# Revit family: 879-002X7X-001-DN450-600
name_source: partatom
category: Pipe Accessories
units: mm (PartAtom-declared; Revit-internal decimal feet)

## family parameters
Always vertical = Yes
Cut with Voids When Loaded = No
Part Type = Valve - Breaks Into
Round Connector Dimension = Use Diameter
Shared = No
Work Plane-Based = No

## types (48) — shared parameters
879-0450-00-04400207299 = DN450_PN10
879-0450-00-044002072A0 = DN450_PN10
879-0450-00-04400217299 = DN450_PN10
879-0450-00-044002172A0 = DN450_PN10
879-0450-00-04400227299 = DN450_PN10
879-0450-00-044002272A0 = DN450_PN10
879-0450-00-04400237299 = DN450_PN10
879-0450-00-044002372A0 = DN450_PN10
879-0450-00-14400207299 = DN450_PN16
879-0450-00-144002072A0 = DN450_PN16
879-0450-00-14400217299 = DN450_PN16
879-0450-00-144002172A0 = DN450_PN16
879-0450-00-14400227299 = DN450_PN16
879-0450-00-144002272A0 = DN450_PN16
879-0450-00-14400237299 = DN450_PN16
879-0450-00-144002372A0 = DN450_PN16
879-0500-00-04400207299 = DN500_PN10
879-0500-00-044002072A0 = DN500_PN10
879-0500-00-04400217299 = DN500_PN10
879-0500-00-044002172A0 = DN500_PN10
879-0500-00-04400227299 = DN500_PN10
879-0500-00-044002272A0 = DN500_PN10
879-0500-00-04400237299 = DN500_PN10
879-0500-00-044002372A0 = DN500_PN10
879-0500-00-14400207299 = DN500_PN16
879-0500-00-144002072A0 = DN500_PN16
879-0500-00-14400217299 = DN500_PN16
879-0500-00-144002172A0 = DN500_PN16
879-0500-00-14400227299 = DN500_PN16
879-0500-00-144002272A0 = DN500_PN16
879-0500-00-14400237299 = DN500_PN16
879-0500-00-144002372A0 = DN500_PN16
879-0600-00-04400207299 = DN600_PN10
879-0600-00-044002072A0 = DN600_PN10
879-0600-00-04400217299 = DN600_PN10
879-0600-00-044002172A0 = DN600_PN10
879-0600-00-04400227299 = DN600_PN10
879-0600-00-044002272A0 = DN600_PN10
879-0600-00-04400237299 = DN600_PN10
879-0600-00-044002372A0 = DN600_PN10
879-0600-00-14400207299 = DN600_PN16
879-0600-00-144002072A0 = DN600_PN16
879-0600-00-14400217299 = DN600_PN16
879-0600-00-144002172A0 = DN600_PN16
879-0600-00-14400227299 = DN600_PN16
879-0600-00-144002272A0 = DN600_PN16
879-0600-00-14400237299 = DN600_PN16
879-0600-00-144002372A0 = DN600_PN16
Body_wall_thickness = 10 mm  [stored 0.0328084 ft]
Bolt_support_Dia = 30 mm  [stored 0.0984252 ft]
Description_ = AVK CONST. FLOW/PRESS. RED. CONTROL VALVE
PG_depth = 21 mm  [stored 0.0688976 ft]
Profile_Dia = 15 mm  [stored 0.0492126 ft]
Profile_Dia_2 = 15 mm  [stored 0.0492126 ft]
Profile_Dia_3 = 30 mm  [stored 0.0984252 ft]
Search_Table = 879-002X7X-001-DN450-600
URL product pages = https://www.avkvalves.com

## per-type parameters (varying)
- 879-0450-00-04400207299_DN450_PN10: A=336.55 mm; Body_Collar_Dia=125 mm; Body_Collar_Dia_2=60 mm  [stored 0.19685 ft]; Body_Flange_Dia=315.79 mm; Body_Flange_Dia_2=324.32 mm; Body_Height_1=300 mm; Body_Height_2=150 mm; Body_Height_3=120 mm; Body_Height_4=165 mm; Body_Top_Dia=37.5 mm; Body_Top_Dia_2=31.25 mm  [stored 0.102526 ft]; Body_With_Dia=266.67 mm; Body_With_Dia_2=266.67 mm; Bolt_support=705.88 mm; Bolt_support_2=352.94 mm; Bolt_support_lenght=245 mm; Bolt_support_lenght_2=255 mm; Bottom_profile=112.5 mm; D1=265 mm; DN=450 mm; FOD=307.5 mm; Fillet_Length=20 mm  [stored 0.0656168 ft]; Flange_thickness=30 mm  [stored 0.0984252 ft]; H3=1060 mm; ID=225 mm; L=1200 mm; L1=1217 mm; L_Ref=1208.5 mm; L_ref_2=541.43 mm; PG_Dia=130 mm; PG_Ref=200 mm; PG_ref=235 mm; Pilot_Dia_1=75.5 mm; Pilot_Dia_1_Ref=90.6 mm; Pilot_Dia_1_Ref_2=181.2 mm; Pilot_Dia_2=143.45 mm; Pilot_Dia_3=50.33 mm; Pilot_Dia_4=25.17 mm; Pilot_Dia_5=16.78 mm; Pilot_top_1=678.75 mm; Pilot_top_ref=73.75 mm  [stored 0.241962 ft]; Profile1_Height=509 mm; Profile1_Length=96.09 mm; Profile1_Length_2=64.06 mm; Top_Profile=423.53 mm; Top_Profile_Ref=428.53 mm; Top_Ref=605 mm; Top_Ref_2=641.88 mm; W=780 mm; W_Ref=636.55 mm
- 879-0450-00-044002072A0_DN450_PN10: A=336.55 mm; Body_Collar_Dia=125 mm; Body_Collar_Dia_2=60 mm  [stored 0.19685 ft]; Body_Flange_Dia=315.79 mm; Body_Flange_Dia_2=324.32 mm; Body_Height_1=300 mm; Body_Height_2=150 mm; Body_Height_3=120 mm; Body_Height_4=165 mm; Body_Top_Dia=37.5 mm; Body_Top_Dia_2=31.25 mm  [stored 0.102526 ft]; Body_With_Dia=266.67 mm; Body_With_Dia_2=266.67 mm; Bolt_support=705.88 mm; Bolt_support_2=352.94 mm; Bolt_support_lenght=245.05 mm; Bolt_support_lenght_2=255.05 mm; Bottom_profile=112.53 mm; D1=265 mm; DN=450.1 mm; FOD=307.5 mm; Fillet_Length=20 mm  [stored 0.0656168 ft]; Flange_thickness=30 mm  [stored 0.0984252 ft]; H3=1220 mm; ID=225.05 mm; L=1200 mm; L1=1217 mm; L_Ref=1208.5 mm; L_ref_2=541.43 mm; PG_Dia=130 mm; PG_Ref=200 mm; PG_ref=235.05 mm; Pilot_Dia_1=75.5 mm; Pilot_Dia_1_Ref=90.6 mm; Pilot_Dia_1_Ref_2=181.2 mm; Pilot_Dia_2=143.45 mm; Pilot_Dia_3=50.33 mm; Pilot_Dia_4=25.17 mm; Pilot_Dia_5=16.78 mm; Pilot_top_1=758.75 mm; Pilot_top_ref=153.75 mm; Profile1_Height=530.5 mm; Profile1_Length=96.09 mm; Profile1_Length_2=64.06 mm; Top_Profile=423.53 mm; Top_Profile_Ref=428.53 mm; Top_Ref=605 mm; Top_Ref_2=681.88 mm; W=780 mm; W_Ref=636.55 mm
- 879-0450-00-04400217299_DN450_PN10: A=329.9 mm; Body_Collar_Dia=125 mm; Body_Collar_Dia_2=60 mm  [stored 0.19685 ft]; Body_Flange_Dia=315.79 mm; Body_Flange_Dia_2=324.32 mm; Body_Height_1=300 mm; Body_Height_2=150 mm; Body_Height_3=120 mm; Body_Height_4=165 mm; Body_Top_Dia=37.5 mm; Body_Top_Dia_2=31.25 mm  [stored 0.102526 ft]; Body_With_Dia=266.67 mm; Body_With_Dia_2=266.67 mm; Bolt_support=705.88 mm; Bolt_support_2=352.94 mm; Bolt_support_lenght=245.1 mm; Bolt_support_lenght_2=255.1 mm; Bottom_profile=112.55 mm; D1=265 mm; DN=450.2 mm; FOD=307.5 mm; Fillet_Length=20 mm  [stored 0.0656168 ft]; Flange_thickness=30 mm  [stored 0.0984252 ft]; H3=1060 mm; ID=225.1 mm; L=1200 mm; L1=1217 mm; L_Ref=1208.5 mm; L_ref_2=541.43 mm; PG_Dia=130 mm; PG_Ref=200 mm; PG_ref=235.1 mm; Pilot_Dia_1=79 mm; Pilot_Dia_1_Ref=94.8 mm; Pilot_Dia_1_Ref_2=189.6 mm; Pilot_Dia_2=150.1 mm; Pilot_Dia_3=52.67 mm; Pilot_Dia_4=26.33 mm; Pilot_Dia_5=17.56 mm; Pilot_top_1=678.75 mm; Pilot_top_ref=73.75 mm  [stored 0.241962 ft]; Profile1_Height=530 mm; Profile1_Length=96.09 mm; Profile1_Length_2=64.06 mm; Top_Profile=423.53 mm; Top_Profile_Ref=428.53 mm; Top_Ref=605 mm; Top_Ref_2=641.88 mm; W=780 mm; W_Ref=629.9 mm
- 879-0450-00-044002172A0_DN450_PN10: A=329.9 mm; Body_Collar_Dia=125 mm; Body_Collar_Dia_2=60 mm  [stored 0.19685 ft]; Body_Flange_Dia=315.79 mm; Body_Flange_Dia_2=324.32 mm; Body_Height_1=300 mm; Body_Height_2=150 mm; Body_Height_3=120 mm; Body_Height_4=165 mm; Body_Top_Dia=37.5 mm; Body_Top_Dia_2=31.25 mm  [stored 0.102526 ft]; Body_With_Dia=266.67 mm; Body_With_Dia_2=266.67 mm; Bolt_support=705.88 mm; Bolt_support_2=352.94 mm; Bolt_support_lenght=245.15 mm; Bolt_support_lenght_2=255.15 mm; Bottom_profile=112.58 mm; D1=265 mm; DN=450.3 mm; FOD=307.5 mm; Fillet_Length=20 mm  [stored 0.0656168 ft]; Flange_thickness=30 mm  [stored 0.0984252 ft]; H3=1220 mm; ID=225.15 mm; L=1200 mm; L1=1217 mm; L_Ref=1208.5 mm; L_ref_2=541.43 mm; PG_Dia=130 mm; PG_Ref=200 mm; PG_ref=235.15 mm; Pilot_Dia_1=79 mm; Pilot_Dia_1_Ref=94.8 mm; Pilot_Dia_1_Ref_2=189.6 mm; Pilot_Dia_2=150.1 mm; Pilot_Dia_3=52.67 mm; Pilot_Dia_4=26.33 mm; Pilot_Dia_5=17.56 mm; Pilot_top_1=758.75 mm; Pilot_top_ref=153.75 mm; Profile1_Height=530.5 mm; Profile1_Length=96.09 mm; Profile1_Length_2=64.06 mm; Top_Profile=423.53 mm; Top_Profile_Ref=428.53 mm; Top_Ref=605 mm; Top_Ref_2=681.88 mm; W=780 mm; W_Ref=629.9 mm
- 879-0450-00-04400227299_DN450_PN10: A=336.55 mm; Body_Collar_Dia=125 mm; Body_Collar_Dia_2=60 mm  [stored 0.19685 ft]; Body_Flange_Dia=315.79 mm; Body_Flange_Dia_2=324.32 mm; Body_Height_1=300 mm; Body_Height_2=150 mm; Body_Height_3=120 mm; Body_Height_4=165 mm; Body_Top_Dia=37.5 mm; Body_Top_Dia_2=31.25 mm  [stored 0.102526 ft]; Body_With_Dia=266.67 mm; Body_With_Dia_2=266.67 mm; Bolt_support=705.88 mm; Bolt_support_2=352.94 mm; Bolt_support_lenght=245.2 mm; Bolt_support_lenght_2=255.2 mm; Bottom_profile=112.6 mm; D1=265 mm; DN=450.4 mm; FOD=307.5 mm; Fillet_Length=20 mm  [stored 0.0656168 ft]; Flange_thickness=30 mm  [stored 0.0984252 ft]; H3=1060 mm; ID=225.2 mm; L=1200 mm; L1=1217 mm; L_Ref=1208.5 mm; L_ref_2=541.43 mm; PG_Dia=130 mm; PG_Ref=200 mm; PG_ref=235.2 mm; Pilot_Dia_1=75.5 mm; Pilot_Dia_1_Ref=90.6 mm; Pilot_Dia_1_Ref_2=181.2 mm; Pilot_Dia_2=143.45 mm; Pilot_Dia_3=50.33 mm; Pilot_Dia_4=25.17 mm; Pilot_Dia_5=16.78 mm; Pilot_top_1=678.75 mm; Pilot_top_ref=73.75 mm  [stored 0.241962 ft]; Profile1_Height=509 mm; Profile1_Length=96.09 mm; Profile1_Length_2=64.06 mm; Top_Profile=423.53 mm; Top_Profile_Ref=428.53 mm; Top_Ref=605 mm; Top_Ref_2=641.88 mm; W=780 mm; W_Ref=636.55 mm
- 879-0450-00-044002272A0_DN450_PN10: A=336.55 mm; Body_Collar_Dia=125 mm; Body_Collar_Dia_2=60 mm  [stored 0.19685 ft]; Body_Flange_Dia=315.79 mm; Body_Flange_Dia_2=324.32 mm; Body_Height_1=300 mm; Body_Height_2=150 mm; Body_Height_3=120 mm; Body_Height_4=165 mm; Body_Top_Dia=37.5 mm; Body_Top_Dia_2=31.25 mm  [stored 0.102526 ft]; Body_With_Dia=266.67 mm; Body_With_Dia_2=266.67 mm; Bolt_support=705.88 mm; Bolt_support_2=352.94 mm; Bolt_support_lenght=245.25 mm; Bolt_support_lenght_2=255.25 mm; Bottom_profile=112.63 mm; D1=265 mm; DN=450.5 mm; FOD=307.5 mm; Fillet_Length=20 mm  [stored 0.0656168 ft]; Flange_thickness=30 mm  [stored 0.0984252 ft]; H3=1220 mm; ID=225.25 mm; L=1200 mm; L1=1217 mm; L_Ref=1208.5 mm; L_ref_2=541.43 mm; PG_Dia=130 mm; PG_Ref=200 mm; PG_ref=235.25 mm; Pilot_Dia_1=75.5 mm; Pilot_Dia_1_Ref=90.6 mm; Pilot_Dia_1_Ref_2=181.2 mm; Pilot_Dia_2=143.45 mm; Pilot_Dia_3=50.33 mm; Pilot_Dia_4=25.17 mm; Pilot_Dia_5=16.78 mm; Pilot_top_1=758.75 mm; Pilot_top_ref=153.75 mm; Profile1_Height=530.5 mm; Profile1_Length=96.09 mm; Profile1_Length_2=64.06 mm; Top_Profile=423.53 mm; Top_Profile_Ref=428.53 mm; Top_Ref=605 mm; Top_Ref_2=681.88 mm; W=780 mm; W_Ref=636.55 mm
- 879-0450-00-04400237299_DN450_PN10: A=329.9 mm; Body_Collar_Dia=125 mm; Body_Collar_Dia_2=60 mm  [stored 0.19685 ft]; Body_Flange_Dia=315.79 mm; Body_Flange_Dia_2=324.32 mm; Body_Height_1=300 mm; Body_Height_2=150 mm; Body_Height_3=120 mm; Body_Height_4=165 mm; Body_Top_Dia=37.5 mm; Body_Top_Dia_2=31.25 mm  [stored 0.102526 ft]; Body_With_Dia=266.67 mm; Body_With_Dia_2=266.67 mm; Bolt_support=705.88 mm; Bolt_support_2=352.94 mm; Bolt_support_lenght=245.3 mm; Bolt_support_lenght_2=255.3 mm; Bottom_profile=112.65 mm; D1=265 mm; DN=450.6 mm; FOD=307.5 mm; Fillet_Length=20 mm  [stored 0.0656168 ft]; Flange_thickness=30 mm  [stored 0.0984252 ft]; H3=1060 mm; ID=225.3 mm; L=1200 mm; L1=1217 mm; L_Ref=1208.5 mm; L_ref_2=541.43 mm; PG_Dia=130 mm; PG_Ref=200 mm; PG_ref=235.3 mm; Pilot_Dia_1=79 mm; Pilot_Dia_1_Ref=94.8 mm; Pilot_Dia_1_Ref_2=189.6 mm; Pilot_Dia_2=150.1 mm; Pilot_Dia_3=52.67 mm; Pilot_Dia_4=26.33 mm; Pilot_Dia_5=17.56 mm; Pilot_top_1=678.75 mm; Pilot_top_ref=73.75 mm  [stored 0.241962 ft]; Profile1_Height=530 mm; Profile1_Length=96.09 mm; Profile1_Length_2=64.06 mm; Top_Profile=423.53 mm; Top_Profile_Ref=428.53 mm; Top_Ref=605 mm; Top_Ref_2=641.88 mm; W=780 mm; W_Ref=629.9 mm
- 879-0450-00-044002372A0_DN450_PN10: A=329.9 mm; Body_Collar_Dia=125 mm; Body_Collar_Dia_2=60 mm  [stored 0.19685 ft]; Body_Flange_Dia=315.79 mm; Body_Flange_Dia_2=324.32 mm; Body_Height_1=300 mm; Body_Height_2=150 mm; Body_Height_3=120 mm; Body_Height_4=165 mm; Body_Top_Dia=37.5 mm; Body_Top_Dia_2=31.25 mm  [stored 0.102526 ft]; Body_With_Dia=266.67 mm; Body_With_Dia_2=266.67 mm; Bolt_support=705.88 mm; Bolt_support_2=352.94 mm; Bolt_support_lenght=245.35 mm; Bolt_support_lenght_2=255.35 mm; Bottom_profile=112.68 mm; D1=265 mm; DN=450.7 mm; FOD=307.5 mm; Fillet_Length=20 mm  [stored 0.0656168 ft]; Flange_thickness=30 mm  [stored 0.0984252 ft]; H3=1220 mm; ID=225.35 mm; L=1200 mm; L1=1217 mm; L_Ref=1208.5 mm; L_ref_2=541.43 mm; PG_Dia=130 mm; PG_Ref=200 mm; PG_ref=235.35 mm; Pilot_Dia_1=79 mm; Pilot_Dia_1_Ref=94.8 mm; Pilot_Dia_1_Ref_2=189.6 mm; Pilot_Dia_2=150.1 mm; Pilot_Dia_3=52.67 mm; Pilot_Dia_4=26.33 mm; Pilot_Dia_5=17.56 mm; Pilot_top_1=758.75 mm; Pilot_top_ref=153.75 mm; Profile1_Height=530.5 mm; Profile1_Length=96.09 mm; Profile1_Length_2=64.06 mm; Top_Profile=423.53 mm; Top_Profile_Ref=428.53 mm; Top_Ref=605 mm; Top_Ref_2=681.88 mm; W=780 mm; W_Ref=629.9 mm
- 879-0450-00-14400207299_DN450_PN16: A=324.05 mm; Body_Collar_Dia=125 mm; Body_Collar_Dia_2=60 mm  [stored 0.19685 ft]; Body_Flange_Dia=315.79 mm; Body_Flange_Dia_2=324.32 mm; Body_Height_1=300 mm; Body_Height_2=150 mm; Body_Height_3=120 mm; Body_Height_4=165 mm; Body_Top_Dia=37.5 mm; Body_Top_Dia_2=31.25 mm  [stored 0.102526 ft]; Body_With_Dia=266.67 mm; Body_With_Dia_2=266.67 mm; Bolt_support=705.88 mm; Bolt_support_2=352.94 mm; Bolt_support_lenght=245.4 mm; Bolt_support_lenght_2=255.4 mm; Bottom_profile=112.7 mm; D1=274 mm; DN=450.8 mm; FOD=320 mm; Fillet_Length=20 mm  [stored 0.0656168 ft]; Flange_thickness=30 mm  [stored 0.0984252 ft]; H3=1060 mm; ID=225.4 mm; L=1200 mm; L1=1217 mm; L_Ref=1208.5 mm; L_ref_2=541.43 mm; PG_Dia=130 mm; PG_Ref=200 mm; PG_ref=235.4 mm; Pilot_Dia_1=75.5 mm; Pilot_Dia_1_Ref=90.6 mm; Pilot_Dia_1_Ref_2=181.2 mm; Pilot_Dia_2=143.45 mm; Pilot_Dia_3=50.33 mm; Pilot_Dia_4=25.17 mm; Pilot_Dia_5=16.78 mm; Pilot_top_1=672.5 mm; Pilot_top_ref=67.5 mm  [stored 0.221457 ft]; Profile1_Height=509 mm; Profile1_Length=100 mm; Profile1_Length_2=66.67 mm; Top_Profile=423.53 mm; Top_Profile_Ref=428.53 mm; Top_Ref=605 mm; Top_Ref_2=638.75 mm; W=780 mm; W_Ref=636.55 mm
- 879-0450-00-144002072A0_DN450_PN16: A=324.05 mm; Body_Collar_Dia=125 mm; Body_Collar_Dia_2=60 mm  [stored 0.19685 ft]; Body_Flange_Dia=315.79 mm; Body_Flange_Dia_2=324.32 mm; Body_Height_1=300 mm; Body_Height_2=150 mm; Body_Height_3=120 mm; Body_Height_4=165 mm; Body_Top_Dia=37.5 mm; Body_Top_Dia_2=31.25 mm  [stored 0.102526 ft]; Body_With_Dia=266.67 mm; Body_With_Dia_2=266.67 mm; Bolt_support=705.88 mm; Bolt_support_2=352.94 mm; Bolt_support_lenght=245.45 mm; Bolt_support_lenght_2=255.45 mm; Bottom_profile=112.73 mm; D1=274 mm; DN=450.9 mm; FOD=320 mm; Fillet_Length=20 mm  [stored 0.0656168 ft]; Flange_thickness=30 mm  [stored 0.0984252 ft]; H3=1220 mm; ID=225.45 mm; L=1200 mm; L1=1217 mm; L_Ref=1208.5 mm; L_ref_2=541.43 mm; PG_Dia=130 mm; PG_Ref=200 mm; PG_ref=235.45 mm; Pilot_Dia_1=75.5 mm; Pilot_Dia_1_Ref=90.6 mm; Pilot_Dia_1_Ref_2=181.2 mm; Pilot_Dia_2=143.45 mm; Pilot_Dia_3=50.33 mm; Pilot_Dia_4=25.17 mm; Pilot_Dia_5=16.78 mm; Pilot_top_1=752.5 mm; Pilot_top_ref=147.5 mm; Profile1_Height=530.5 mm; Profile1_Length=100 mm; Profile1_Length_2=66.67 mm; Top_Profile=423.53 mm; Top_Profile_Ref=428.53 mm; Top_Ref=605 mm; Top_Ref_2=678.75 mm; W=780 mm; W_Ref=636.55 mm
- 879-0450-00-14400217299_DN450_PN16: A=317.4 mm; Body_Collar_Dia=125 mm; Body_Collar_Dia_2=60 mm  [stored 0.19685 ft]; Body_Flange_Dia=315.79 mm; Body_Flange_Dia_2=324.32 mm; Body_Height_1=300 mm; Body_Height_2=150 mm; Body_Height_3=120 mm; Body_Height_4=165 mm; Body_Top_Dia=37.5 mm; Body_Top_Dia_2=31.25 mm  [stored 0.102526 ft]; Body_With_Dia=266.67 mm; Body_With_Dia_2=266.67 mm; Bolt_support=705.88 mm; Bolt_support_2=352.94 mm; Bolt_support_lenght=245.06 mm; Bolt_support_lenght_2=255.06 mm; Bottom_profile=112.53 mm; D1=274 mm; DN=450.11 mm; FOD=320 mm; Fillet_Length=20 mm  [stored 0.0656168 ft]; Flange_thickness=30 mm  [stored 0.0984252 ft]; H3=1060 mm; ID=225.06 mm; L=1200 mm; L1=1217 mm; L_Ref=1208.5 mm; L_ref_2=541.43 mm; PG_Dia=130 mm; PG_Ref=200 mm; PG_ref=235.06 mm; Pilot_Dia_1=79 mm; Pilot_Dia_1_Ref=94.8 mm; Pilot_Dia_1_Ref_2=189.6 mm; Pilot_Dia_2=150.1 mm; Pilot_Dia_3=52.67 mm; Pilot_Dia_4=26.33 mm; Pilot_Dia_5=17.56 mm; Pilot_top_1=672.5 mm; Pilot_top_ref=67.5 mm  [stored 0.221457 ft]; Profile1_Height=530 mm; Profile1_Length=100 mm; Profile1_Length_2=66.67 mm; Top_Profile=423.53 mm; Top_Profile_Ref=428.53 mm; Top_Ref=605 mm; Top_Ref_2=638.75 mm; W=780 mm; W_Ref=629.9 mm
- 879-0450-00-144002172A0_DN450_PN16: A=317.4 mm; Body_Collar_Dia=125 mm; Body_Collar_Dia_2=60 mm  [stored 0.19685 ft]; Body_Flange_Dia=315.79 mm; Body_Flange_Dia_2=324.32 mm; Body_Height_1=300 mm; Body_Height_2=150 mm; Body_Height_3=120 mm; Body_Height_4=165 mm; Body_Top_Dia=37.5 mm; Body_Top_Dia_2=31.25 mm  [stored 0.102526 ft]; Body_With_Dia=266.67 mm; Body_With_Dia_2=266.67 mm; Bolt_support=705.88 mm; Bolt_support_2=352.94 mm; Bolt_support_lenght=245.06 mm; Bolt_support_lenght_2=255.06 mm; Bottom_profile=112.53 mm; D1=274 mm; DN=450.12 mm; FOD=320 mm; Fillet_Length=20 mm  [stored 0.0656168 ft]; Flange_thickness=30 mm  [stored 0.0984252 ft]; H3=1220 mm; ID=225.06 mm; L=1200 mm; L1=1217 mm; L_Ref=1208.5 mm; L_ref_2=541.43 mm; PG_Dia=130 mm; PG_Ref=200 mm; PG_ref=235.06 mm; Pilot_Dia_1=79 mm; Pilot_Dia_1_Ref=94.8 mm; Pilot_Dia_1_Ref_2=189.6 mm; Pilot_Dia_2=150.1 mm; Pilot_Dia_3=52.67 mm; Pilot_Dia_4=26.33 mm; Pilot_Dia_5=17.56 mm; Pilot_top_1=752.5 mm; Pilot_top_ref=147.5 mm; Profile1_Height=530.5 mm; Profile1_Length=100 mm; Profile1_Length_2=66.67 mm; Top_Profile=423.53 mm; Top_Profile_Ref=428.53 mm; Top_Ref=605 mm; Top_Ref_2=678.75 mm; W=780 mm; W_Ref=629.9 mm
- 879-0450-00-14400227299_DN450_PN16: A=324.05 mm; Body_Collar_Dia=125 mm; Body_Collar_Dia_2=60 mm  [stored 0.19685 ft]; Body_Flange_Dia=315.79 mm; Body_Flange_Dia_2=324.32 mm; Body_Height_1=300 mm; Body_Height_2=150 mm; Body_Height_3=120 mm; Body_Height_4=165 mm; Body_Top_Dia=37.5 mm; Body_Top_Dia_2=31.25 mm  [stored 0.102526 ft]; Body_With_Dia=266.67 mm; Body_With_Dia_2=266.67 mm; Bolt_support=705.88 mm; Bolt_support_2=352.94 mm; Bolt_support_lenght=245.07 mm; Bolt_support_lenght_2=255.07 mm; Bottom_profile=112.53 mm; D1=274 mm; DN=450.13 mm; FOD=320 mm; Fillet_Length=20 mm  [stored 0.0656168 ft]; Flange_thickness=30 mm  [stored 0.0984252 ft]; H3=1060 mm; ID=225.07 mm; L=1200 mm; L1=1217 mm; L_Ref=1208.5 mm; L_ref_2=541.43 mm; PG_Dia=130 mm; PG_Ref=200 mm; PG_ref=235.07 mm; Pilot_Dia_1=75.5 mm; Pilot_Dia_1_Ref=90.6 mm; Pilot_Dia_1_Ref_2=181.2 mm; Pilot_Dia_2=143.45 mm; Pilot_Dia_3=50.33 mm; Pilot_Dia_4=25.17 mm; Pilot_Dia_5=16.78 mm; Pilot_top_1=672.5 mm; Pilot_top_ref=67.5 mm  [stored 0.221457 ft]; Profile1_Height=509 mm; Profile1_Length=100 mm; Profile1_Length_2=66.67 mm; Top_Profile=423.53 mm; Top_Profile_Ref=428.53 mm; Top_Ref=605 mm; Top_Ref_2=638.75 mm; W=780 mm; W_Ref=636.55 mm
- 879-0450-00-144002272A0_DN450_PN16: A=324.05 mm; Body_Collar_Dia=125 mm; Body_Collar_Dia_2=60 mm  [stored 0.19685 ft]; Body_Flange_Dia=315.79 mm; Body_Flange_Dia_2=324.32 mm; Body_Height_1=300 mm; Body_Height_2=150 mm; Body_Height_3=120 mm; Body_Height_4=165 mm; Body_Top_Dia=37.5 mm; Body_Top_Dia_2=31.25 mm  [stored 0.102526 ft]; Body_With_Dia=266.67 mm; Body_With_Dia_2=266.67 mm; Bolt_support=705.88 mm; Bolt_support_2=352.94 mm; Bolt_support_lenght=245.07 mm; Bolt_support_lenght_2=255.07 mm; Bottom_profile=112.54 mm; D1=274 mm; DN=450.14 mm; FOD=320 mm; Fillet_Length=20 mm  [stored 0.0656168 ft]; Flange_thickness=30 mm  [stored 0.0984252 ft]; H3=1220 mm; ID=225.07 mm; L=1200 mm; L1=1217 mm; L_Ref=1208.5 mm; L_ref_2=541.43 mm; PG_Dia=130 mm; PG_Ref=200 mm; PG_ref=235.07 mm; Pilot_Dia_1=75.5 mm; Pilot_Dia_1_Ref=90.6 mm; Pilot_Dia_1_Ref_2=181.2 mm; Pilot_Dia_2=143.45 mm; Pilot_Dia_3=50.33 mm; Pilot_Dia_4=25.17 mm; Pilot_Dia_5=16.78 mm; Pilot_top_1=752.5 mm; Pilot_top_ref=147.5 mm; Profile1_Height=530.5 mm; Profile1_Length=100 mm; Profile1_Length_2=66.67 mm; Top_Profile=423.53 mm; Top_Profile_Ref=428.53 mm; Top_Ref=605 mm; Top_Ref_2=678.75 mm; W=780 mm; W_Ref=636.55 mm
- 879-0450-00-14400237299_DN450_PN16: A=317.4 mm; Body_Collar_Dia=125 mm; Body_Collar_Dia_2=60 mm  [stored 0.19685 ft]; Body_Flange_Dia=315.79 mm; Body_Flange_Dia_2=324.32 mm; Body_Height_1=300 mm; Body_Height_2=150 mm; Body_Height_3=120 mm; Body_Height_4=165 mm; Body_Top_Dia=37.5 mm; Body_Top_Dia_2=31.25 mm  [stored 0.102526 ft]; Body_With_Dia=266.67 mm; Body_With_Dia_2=266.67 mm; Bolt_support=705.88 mm; Bolt_support_2=352.94 mm; Bolt_support_lenght=245.08 mm; Bolt_support_lenght_2=255.08 mm; Bottom_profile=112.54 mm; D1=274 mm; DN=450.15 mm; FOD=320 mm; Fillet_Length=20 mm  [stored 0.0656168 ft]; Flange_thickness=30 mm  [stored 0.0984252 ft]; H3=1060 mm; ID=225.08 mm; L=1200 mm; L1=1217 mm; L_Ref=1208.5 mm; L_ref_2=541.43 mm; PG_Dia=130 mm; PG_Ref=200 mm; PG_ref=235.08 mm; Pilot_Dia_1=79 mm; Pilot_Dia_1_Ref=94.8 mm; Pilot_Dia_1_Ref_2=189.6 mm; Pilot_Dia_2=150.1 mm; Pilot_Dia_3=52.67 mm; Pilot_Dia_4=26.33 mm; Pilot_Dia_5=17.56 mm; Pilot_top_1=672.5 mm; Pilot_top_ref=67.5 mm  [stored 0.221457 ft]; Profile1_Height=530 mm; Profile1_Length=100 mm; Profile1_Length_2=66.67 mm; Top_Profile=423.53 mm; Top_Profile_Ref=428.53 mm; Top_Ref=605 mm; Top_Ref_2=638.75 mm; W=780 mm; W_Ref=629.9 mm
- 879-0450-00-144002372A0_DN450_PN16: A=317.4 mm; Body_Collar_Dia=125 mm; Body_Collar_Dia_2=60 mm  [stored 0.19685 ft]; Body_Flange_Dia=315.79 mm; Body_Flange_Dia_2=324.32 mm; Body_Height_1=300 mm; Body_Height_2=150 mm; Body_Height_3=120 mm; Body_Height_4=165 mm; Body_Top_Dia=37.5 mm; Body_Top_Dia_2=31.25 mm  [stored 0.102526 ft]; Body_With_Dia=266.67 mm; Body_With_Dia_2=266.67 mm; Bolt_support=705.88 mm; Bolt_support_2=352.94 mm; Bolt_support_lenght=245.08 mm; Bolt_support_lenght_2=255.08 mm; Bottom_profile=112.54 mm; D1=274 mm; DN=450.16 mm; FOD=320 mm; Fillet_Length=20 mm  [stored 0.0656168 ft]; Flange_thickness=30 mm  [stored 0.0984252 ft]; H3=1220 mm; ID=225.08 mm; L=1200 mm; L1=1217 mm; L_Ref=1208.5 mm; L_ref_2=541.43 mm; PG_Dia=130 mm; PG_Ref=200 mm; PG_ref=235.08 mm; Pilot_Dia_1=79 mm; Pilot_Dia_1_Ref=94.8 mm; Pilot_Dia_1_Ref_2=189.6 mm; Pilot_Dia_2=150.1 mm; Pilot_Dia_3=52.67 mm; Pilot_Dia_4=26.33 mm; Pilot_Dia_5=17.56 mm; Pilot_top_1=752.5 mm; Pilot_top_ref=147.5 mm; Profile1_Height=530.5 mm; Profile1_Length=100 mm; Profile1_Length_2=66.67 mm; Top_Profile=423.53 mm; Top_Profile_Ref=428.53 mm; Top_Ref=605 mm; Top_Ref_2=678.75 mm; W=780 mm; W_Ref=629.9 mm
- 879-0500-00-04400207299_DN500_PN10: A=444.8 mm; Body_Collar_Dia=130.21 mm; Body_Collar_Dia_2=62.5 mm  [stored 0.205052 ft]; Body_Flange_Dia=328.95 mm; Body_Flange_Dia_2=337.84 mm; Body_Height_1=312.5 mm; Body_Height_2=156.25 mm; Body_Height_3=125 mm; Body_Height_4=171.25 mm; Body_Top_Dia=39.06 mm; Body_Top_Dia_2=32.55 mm; Body_With_Dia=277.78 mm; Body_With_Dia_2=277.78 mm; Bolt_support=735.29 mm; Bolt_support_2=367.65 mm; Bolt_support_lenght=270 mm; Bolt_support_lenght_2=280 mm; Bottom_profile=125 mm; D1=291 mm; DN=500 mm; FOD=335 mm; Fillet_Length=25 mm  [stored 0.082021 ft]; Flange_thickness=31.5 mm  [stored 0.103346 ft]; H3=1245 mm; ID=250 mm; L=1250 mm; L1=1267 mm; L_Ref=1258.5 mm; L_ref_2=563.74 mm; PG_Dia=130 mm; PG_Ref=208.33 mm; PG_ref=260 mm; Pilot_Dia_1=83 mm; Pilot_Dia_1_Ref=99.6 mm; Pilot_Dia_1_Ref_2=199.2 mm; Pilot_Dia_2=157.7 mm; Pilot_Dia_3=55.33 mm; Pilot_Dia_4=27.67 mm; Pilot_Dia_5=18.44 mm; Pilot_top_1=769.38 mm; Pilot_top_ref=140.63 mm; Profile1_Height=541 mm; Profile1_Length=104.69 mm; Profile1_Length_2=69.79 mm; Top_Profile=441.18 mm; Top_Profile_Ref=446.18 mm; Top_Ref=628.75 mm; Top_Ref_2=699.06 mm; W=930 mm; W_Ref=772.3 mm
- 879-0500-00-044002072A0_DN500_PN10: A=444.8 mm; Body_Collar_Dia=130.21 mm; Body_Collar_Dia_2=62.5 mm  [stored 0.205052 ft]; Body_Flange_Dia=328.95 mm; Body_Flange_Dia_2=337.84 mm; Body_Height_1=312.5 mm; Body_Height_2=156.25 mm; Body_Height_3=125 mm; Body_Height_4=171.25 mm; Body_Top_Dia=39.06 mm; Body_Top_Dia_2=32.55 mm; Body_With_Dia=277.78 mm; Body_With_Dia_2=277.78 mm; Bolt_support=735.29 mm; Bolt_support_2=367.65 mm; Bolt_support_lenght=270.05 mm; Bolt_support_lenght_2=280.05 mm; Bottom_profile=125.03 mm; D1=291 mm; DN=500.1 mm; FOD=335 mm; Fillet_Length=25 mm  [stored 0.082021 ft]; Flange_thickness=31.5 mm  [stored 0.103346 ft]; H3=1408 mm; ID=250.05 mm; L=1250 mm; L1=1267 mm; L_Ref=1258.5 mm; L_ref_2=563.74 mm; PG_Dia=130 mm; PG_Ref=208.33 mm; PG_ref=260.05 mm; Pilot_Dia_1=83 mm; Pilot_Dia_1_Ref=99.6 mm; Pilot_Dia_1_Ref_2=199.2 mm; Pilot_Dia_2=157.7 mm; Pilot_Dia_3=55.33 mm; Pilot_Dia_4=27.67 mm; Pilot_Dia_5=18.44 mm; Pilot_top_1=850.88 mm; Pilot_top_ref=222.13 mm; Profile1_Height=541 mm; Profile1_Length=104.69 mm; Profile1_Length_2=69.79 mm; Top_Profile=441.18 mm; Top_Profile_Ref=446.18 mm; Top_Ref=628.75 mm; Top_Ref_2=739.81 mm; W=930 mm; W_Ref=772.3 mm
- 879-0500-00-04400217299_DN500_PN10: A=433.4 mm; Body_Collar_Dia=130.21 mm; Body_Collar_Dia_2=62.5 mm  [stored 0.205052 ft]; Body_Flange_Dia=328.95 mm; Body_Flange_Dia_2=337.84 mm; Body_Height_1=312.5 mm; Body_Height_2=156.25 mm; Body_Height_3=125 mm; Body_Height_4=171.25 mm; Body_Top_Dia=39.06 mm; Body_Top_Dia_2=32.55 mm; Body_With_Dia=277.78 mm; Body_With_Dia_2=277.78 mm; Bolt_support=735.29 mm; Bolt_support_2=367.65 mm; Bolt_support_lenght=270.1 mm; Bolt_support_lenght_2=280.1 mm; Bottom_profile=125.05 mm; D1=291 mm; DN=500.2 mm; FOD=335 mm; Fillet_Length=25 mm  [stored 0.082021 ft]; Flange_thickness=31.5 mm  [stored 0.103346 ft]; H3=1245 mm; ID=250.1 mm; L=1250 mm; L1=1267 mm; L_Ref=1258.5 mm; L_ref_2=563.74 mm; PG_Dia=130 mm; PG_Ref=208.33 mm; PG_ref=260.1 mm; Pilot_Dia_1=89 mm; Pilot_Dia_1_Ref=106.8 mm; Pilot_Dia_1_Ref_2=213.6 mm; Pilot_Dia_2=169.1 mm; Pilot_Dia_3=59.33 mm; Pilot_Dia_4=29.67 mm; Pilot_Dia_5=19.78 mm; Pilot_top_1=769.38 mm; Pilot_top_ref=140.63 mm; Profile1_Height=541 mm; Profile1_Length=104.69 mm; Profile1_Length_2=69.79 mm; Top_Profile=441.18 mm; Top_Profile_Ref=446.18 mm; Top_Ref=628.75 mm; Top_Ref_2=699.06 mm; W=930 mm; W_Ref=760.9 mm
- 879-0500-00-04400227299_DN500_PN10: A=444.8 mm; Body_Collar_Dia=130.21 mm; Body_Collar_Dia_2=62.5 mm  [stored 0.205052 ft]; Body_Flange_Dia=328.95 mm; Body_Flange_Dia_2=337.84 mm; Body_Height_1=312.5 mm; Body_Height_2=156.25 mm; Body_Height_3=125 mm; Body_Height_4=171.25 mm; Body_Top_Dia=39.06 mm; Body_Top_Dia_2=32.55 mm; Body_With_Dia=277.78 mm; Body_With_Dia_2=277.78 mm; Bolt_support=735.29 mm; Bolt_support_2=367.65 mm; Bolt_support_lenght=270.2 mm; Bolt_support_lenght_2=280.2 mm; Bottom_profile=125.1 mm; D1=291 mm; DN=500.4 mm; FOD=335 mm; Fillet_Length=25 mm  [stored 0.082021 ft]; Flange_thickness=31.5 mm  [stored 0.103346 ft]; H3=1245 mm; ID=250.2 mm; L=1250 mm; L1=1267 mm; L_Ref=1258.5 mm; L_ref_2=563.74 mm; PG_Dia=130 mm; PG_Ref=208.33 mm; PG_ref=260.2 mm; Pilot_Dia_1=83 mm; Pilot_Dia_1_Ref=99.6 mm; Pilot_Dia_1_Ref_2=199.2 mm; Pilot_Dia_2=157.7 mm; Pilot_Dia_3=55.33 mm; Pilot_Dia_4=27.67 mm; Pilot_Dia_5=18.44 mm; Pilot_top_1=769.38 mm; Pilot_top_ref=140.63 mm; Profile1_Height=541 mm; Profile1_Length=104.69 mm; Profile1_Length_2=69.79 mm; Top_Profile=441.18 mm; Top_Profile_Ref=446.18 mm; Top_Ref=628.75 mm; Top_Ref_2=699.06 mm; W=930 mm; W_Ref=772.3 mm
- 879-0500-00-044002272A0_DN500_PN10: A=444.8 mm; Body_Collar_Dia=130.21 mm; Body_Collar_Dia_2=62.5 mm  [stored 0.205052 ft]; Body_Flange_Dia=328.95 mm; Body_Flange_Dia_2=337.84 mm; Body_Height_1=312.5 mm; Body_Height_2=156.25 mm; Body_Height_3=125 mm; Body_Height_4=171.25 mm; Body_Top_Dia=39.06 mm; Body_Top_Dia_2=32.55 mm; Body_With_Dia=277.78 mm; Body_With_Dia_2=277.78 mm; Bolt_support=735.29 mm; Bolt_support_2=367.65 mm; Bolt_support_lenght=270.25 mm; Bolt_support_lenght_2=280.25 mm; Bottom_profile=125.13 mm; D1=291 mm; DN=500.5 mm; FOD=335 mm; Fillet_Length=25 mm  [stored 0.082021 ft]; Flange_thickness=31.5 mm  [stored 0.103346 ft]; H3=1408 mm; ID=250.25 mm; L=1250 mm; L1=1267 mm; L_Ref=1258.5 mm; L_ref_2=563.74 mm; PG_Dia=130 mm; PG_Ref=208.33 mm; PG_ref=260.25 mm; Pilot_Dia_1=83 mm; Pilot_Dia_1_Ref=99.6 mm; Pilot_Dia_1_Ref_2=199.2 mm; Pilot_Dia_2=157.7 mm; Pilot_Dia_3=55.33 mm; Pilot_Dia_4=27.67 mm; Pilot_Dia_5=18.44 mm; Pilot_top_1=850.88 mm; Pilot_top_ref=222.13 mm; Profile1_Height=541 mm; Profile1_Length=104.69 mm; Profile1_Length_2=69.79 mm; Top_Profile=441.18 mm; Top_Profile_Ref=446.18 mm; Top_Ref=628.75 mm; Top_Ref_2=739.81 mm; W=930 mm; W_Ref=772.3 mm
- 879-0500-00-04400237299_DN500_PN10: A=433.4 mm; Body_Collar_Dia=130.21 mm; Body_Collar_Dia_2=62.5 mm  [stored 0.205052 ft]; Body_Flange_Dia=328.95 mm; Body_Flange_Dia_2=337.84 mm; Body_Height_1=312.5 mm; Body_Height_2=156.25 mm; Body_Height_3=125 mm; Body_Height_4=171.25 mm; Body_Top_Dia=39.06 mm; Body_Top_Dia_2=32.55 mm; Body_With_Dia=277.78 mm; Body_With_Dia_2=277.78 mm; Bolt_support=735.29 mm; Bolt_support_2=367.65 mm; Bolt_support_lenght=270.3 mm; Bolt_support_lenght_2=280.3 mm; Bottom_profile=125.15 mm; D1=291 mm; DN=500.6 mm; FOD=335 mm; Fillet_Length=25 mm  [stored 0.082021 ft]; Flange_thickness=31.5 mm  [stored 0.103346 ft]; H3=1245 mm; ID=250.3 mm; L=1250 mm; L1=1267 mm; L_Ref=1258.5 mm; L_ref_2=563.74 mm; PG_Dia=130 mm; PG_Ref=208.33 mm; PG_ref=260.3 mm; Pilot_Dia_1=89 mm; Pilot_Dia_1_Ref=106.8 mm; Pilot_Dia_1_Ref_2=213.6 mm; Pilot_Dia_2=169.1 mm; Pilot_Dia_3=59.33 mm; Pilot_Dia_4=29.67 mm; Pilot_Dia_5=19.78 mm; Pilot_top_1=769.38 mm; Pilot_top_ref=140.63 mm; Profile1_Height=541 mm; Profile1_Length=104.69 mm; Profile1_Length_2=69.79 mm; Top_Profile=441.18 mm; Top_Profile_Ref=446.18 mm; Top_Ref=628.75 mm; Top_Ref_2=699.06 mm; W=930 mm; W_Ref=760.9 mm
- 879-0500-00-044002372A0_DN500_PN10: A=433.4 mm; Body_Collar_Dia=130.21 mm; Body_Collar_Dia_2=62.5 mm  [stored 0.205052 ft]; Body_Flange_Dia=328.95 mm; Body_Flange_Dia_2=337.84 mm; Body_Height_1=312.5 mm; Body_Height_2=156.25 mm; Body_Height_3=125 mm; Body_Height_4=171.25 mm; Body_Top_Dia=39.06 mm; Body_Top_Dia_2=32.55 mm; Body_With_Dia=277.78 mm; Body_With_Dia_2=277.78 mm; Bolt_support=735.29 mm; Bolt_support_2=367.65 mm; Bolt_support_lenght=270.35 mm; Bolt_support_lenght_2=280.35 mm; Bottom_profile=125.18 mm; D1=291 mm; DN=500.7 mm; FOD=335 mm; Fillet_Length=25 mm  [stored 0.082021 ft]; Flange_thickness=31.5 mm  [stored 0.103346 ft]; H3=1408 mm; ID=250.35 mm; L=1250 mm; L1=1267 mm; L_Ref=1258.5 mm; L_ref_2=563.74 mm; PG_Dia=130 mm; PG_Ref=208.33 mm; PG_ref=260.35 mm; Pilot_Dia_1=89 mm; Pilot_Dia_1_Ref=106.8 mm; Pilot_Dia_1_Ref_2=213.6 mm; Pilot_Dia_2=169.1 mm; Pilot_Dia_3=59.33 mm; Pilot_Dia_4=29.67 mm; Pilot_Dia_5=19.78 mm; Pilot_top_1=850.88 mm; Pilot_top_ref=222.13 mm; Profile1_Height=563 mm; Profile1_Length=104.69 mm; Profile1_Length_2=69.79 mm; Top_Profile=441.18 mm; Top_Profile_Ref=446.18 mm; Top_Ref=628.75 mm; Top_Ref_2=739.81 mm; W=930 mm; W_Ref=760.9 mm
- 879-0500-00-14400207299_DN500_PN16: A=422.3 mm; Body_Collar_Dia=130.21 mm; Body_Collar_Dia_2=62.5 mm  [stored 0.205052 ft]; Body_Flange_Dia=328.95 mm; Body_Flange_Dia_2=337.84 mm; Body_Height_1=312.5 mm; Body_Height_2=156.25 mm; Body_Height_3=125 mm; Body_Height_4=171.25 mm; Body_Top_Dia=39.06 mm; Body_Top_Dia_2=32.55 mm; Body_With_Dia=277.78 mm; Body_With_Dia_2=277.78 mm; Bolt_support=735.29 mm; Bolt_support_2=367.65 mm; Bolt_support_lenght=270.4 mm; Bolt_support_lenght_2=280.4 mm; Bottom_profile=125.2 mm; D1=304.5 mm; DN=500.8 mm; FOD=357.5 mm; Fillet_Length=25 mm  [stored 0.082021 ft]; Flange_thickness=31.5 mm  [stored 0.103346 ft]; H3=1245 mm; ID=250.4 mm; L=1250 mm; L1=1267 mm; L_Ref=1258.5 mm; L_ref_2=563.74 mm; PG_Dia=130 mm; PG_Ref=208.33 mm; PG_ref=260.4 mm; Pilot_Dia_1=83 mm; Pilot_Dia_1_Ref=99.6 mm; Pilot_Dia_1_Ref_2=199.2 mm; Pilot_Dia_2=157.7 mm; Pilot_Dia_3=55.33 mm; Pilot_Dia_4=27.67 mm; Pilot_Dia_5=18.44 mm; Pilot_top_1=758.13 mm; Pilot_top_ref=129.38 mm; Profile1_Height=541 mm; Profile1_Length=111.72 mm; Profile1_Length_2=74.48 mm; Top_Profile=441.18 mm; Top_Profile_Ref=446.18 mm; Top_Ref=628.75 mm; Top_Ref_2=693.44 mm; W=930 mm; W_Ref=772.3 mm
- 879-0500-00-144002072A0_DN500_PN16: A=422.3 mm; Body_Collar_Dia=130.21 mm; Body_Collar_Dia_2=62.5 mm  [stored 0.205052 ft]; Body_Flange_Dia=328.95 mm; Body_Flange_Dia_2=337.84 mm; Body_Height_1=312.5 mm; Body_Height_2=156.25 mm; Body_Height_3=125 mm; Body_Height_4=171.25 mm; Body_Top_Dia=39.06 mm; Body_Top_Dia_2=32.55 mm; Body_With_Dia=277.78 mm; Body_With_Dia_2=277.78 mm; Bolt_support=735.29 mm; Bolt_support_2=367.65 mm; Bolt_support_lenght=270.45 mm; Bolt_support_lenght_2=280.45 mm; Bottom_profile=125.23 mm; D1=304.5 mm; DN=500.9 mm; FOD=357.5 mm; Fillet_Length=25 mm  [stored 0.082021 ft]; Flange_thickness=31.5 mm  [stored 0.103346 ft]; H3=1408 mm; ID=250.45 mm; L=1250 mm; L1=1267 mm; L_Ref=1258.5 mm; L_ref_2=563.74 mm; PG_Dia=130 mm; PG_Ref=208.33 mm; PG_ref=260.45 mm; Pilot_Dia_1=83 mm; Pilot_Dia_1_Ref=99.6 mm; Pilot_Dia_1_Ref_2=199.2 mm; Pilot_Dia_2=157.7 mm; Pilot_Dia_3=55.33 mm; Pilot_Dia_4=27.67 mm; Pilot_Dia_5=18.44 mm; Pilot_top_1=839.63 mm; Pilot_top_ref=210.88 mm; Profile1_Height=541 mm; Profile1_Length=111.72 mm; Profile1_Length_2=74.48 mm; Top_Profile=441.18 mm; Top_Profile_Ref=446.18 mm; Top_Ref=628.75 mm; Top_Ref_2=734.19 mm; W=930 mm; W_Ref=772.3 mm
- 879-0500-00-14400217299_DN500_PN16: A=410.9 mm; Body_Collar_Dia=130.21 mm; Body_Collar_Dia_2=62.5 mm  [stored 0.205052 ft]; Body_Flange_Dia=328.95 mm; Body_Flange_Dia_2=337.84 mm; Body_Height_1=312.5 mm; Body_Height_2=156.25 mm; Body_Height_3=125 mm; Body_Height_4=171.25 mm; Body_Top_Dia=39.06 mm; Body_Top_Dia_2=32.55 mm; Body_With_Dia=277.78 mm; Body_With_Dia_2=277.78 mm; Bolt_support=735.29 mm; Bolt_support_2=367.65 mm; Bolt_support_lenght=270.06 mm; Bolt_support_lenght_2=280.06 mm; Bottom_profile=125.03 mm; D1=304.5 mm; DN=500.11 mm; FOD=357.5 mm; Fillet_Length=25 mm  [stored 0.082021 ft]; Flange_thickness=31.5 mm  [stored 0.103346 ft]; H3=1245 mm; ID=250.06 mm; L=1250 mm; L1=1267 mm; L_Ref=1258.5 mm; L_ref_2=563.74 mm; PG_Dia=130 mm; PG_Ref=208.33 mm; PG_ref=260.06 mm; Pilot_Dia_1=89 mm; Pilot_Dia_1_Ref=106.8 mm; Pilot_Dia_1_Ref_2=213.6 mm; Pilot_Dia_2=169.1 mm; Pilot_Dia_3=59.33 mm; Pilot_Dia_4=29.67 mm; Pilot_Dia_5=19.78 mm; Pilot_top_1=758.13 mm; Pilot_top_ref=129.38 mm; Profile1_Height=541 mm; Profile1_Length=111.72 mm; Profile1_Length_2=74.48 mm; Top_Profile=441.18 mm; Top_Profile_Ref=446.18 mm; Top_Ref=628.75 mm; Top_Ref_2=693.44 mm; W=930 mm; W_Ref=760.9 mm
- 879-0500-00-144002172A0_DN500_PN16: A=410.9 mm; Body_Collar_Dia=130.21 mm; Body_Collar_Dia_2=62.5 mm  [stored 0.205052 ft]; Body_Flange_Dia=328.95 mm; Body_Flange_Dia_2=337.84 mm; Body_Height_1=312.5 mm; Body_Height_2=156.25 mm; Body_Height_3=125 mm; Body_Height_4=171.25 mm; Body_Top_Dia=39.06 mm; Body_Top_Dia_2=32.55 mm; Body_With_Dia=277.78 mm; Body_With_Dia_2=277.78 mm; Bolt_support=735.29 mm; Bolt_support_2=367.65 mm; Bolt_support_lenght=270.06 mm; Bolt_support_lenght_2=280.06 mm; Bottom_profile=125.03 mm; D1=304.5 mm; DN=500.12 mm; FOD=357.5 mm; Fillet_Length=25 mm  [stored 0.082021 ft]; Flange_thickness=31.5 mm  [stored 0.103346 ft]; H3=1408 mm; ID=250.06 mm; L=1250 mm; L1=1267 mm; L_Ref=1258.5 mm; L_ref_2=563.74 mm; PG_Dia=130 mm; PG_Ref=208.33 mm; PG_ref=260.06 mm; Pilot_Dia_1=89 mm; Pilot_Dia_1_Ref=106.8 mm; Pilot_Dia_1_Ref_2=213.6 mm; Pilot_Dia_2=169.1 mm; Pilot_Dia_3=59.33 mm; Pilot_Dia_4=29.67 mm; Pilot_Dia_5=19.78 mm; Pilot_top_1=839.63 mm; Pilot_top_ref=210.88 mm; Profile1_Height=563 mm; Profile1_Length=111.72 mm; Profile1_Length_2=74.48 mm; Top_Profile=441.18 mm; Top_Profile_Ref=446.18 mm; Top_Ref=628.75 mm; Top_Ref_2=734.19 mm; W=930 mm; W_Ref=760.9 mm
- 879-0500-00-14400227299_DN500_PN16: A=422.3 mm; Body_Collar_Dia=130.21 mm; Body_Collar_Dia_2=62.5 mm  [stored 0.205052 ft]; Body_Flange_Dia=328.95 mm; Body_Flange_Dia_2=337.84 mm; Body_Height_1=312.5 mm; Body_Height_2=156.25 mm; Body_Height_3=125 mm; Body_Height_4=171.25 mm; Body_Top_Dia=39.06 mm; Body_Top_Dia_2=32.55 mm; Body_With_Dia=277.78 mm; Body_With_Dia_2=277.78 mm; Bolt_support=735.29 mm; Bolt_support_2=367.65 mm; Bolt_support_lenght=270.07 mm; Bolt_support_lenght_2=280.07 mm; Bottom_profile=125.03 mm; D1=304.5 mm; DN=500.13 mm; FOD=357.5 mm; Fillet_Length=25 mm  [stored 0.082021 ft]; Flange_thickness=31.5 mm  [stored 0.103346 ft]; H3=1245 mm; ID=250.07 mm; L=1250 mm; L1=1267 mm; L_Ref=1258.5 mm; L_ref_2=563.74 mm; PG_Dia=130 mm; PG_Ref=208.33 mm; PG_ref=260.07 mm; Pilot_Dia_1=83 mm; Pilot_Dia_1_Ref=99.6 mm; Pilot_Dia_1_Ref_2=199.2 mm; Pilot_Dia_2=157.7 mm; Pilot_Dia_3=55.33 mm; Pilot_Dia_4=27.67 mm; Pilot_Dia_5=18.44 mm; Pilot_top_1=758.13 mm; Pilot_top_ref=129.38 mm; Profile1_Height=541 mm; Profile1_Length=111.72 mm; Profile1_Length_2=74.48 mm; Top_Profile=441.18 mm; Top_Profile_Ref=446.18 mm; Top_Ref=628.75 mm; Top_Ref_2=693.44 mm; W=930 mm; W_Ref=772.3 mm
- 879-0500-00-144002272A0_DN500_PN16: A=422.3 mm; Body_Collar_Dia=130.21 mm; Body_Collar_Dia_2=62.5 mm  [stored 0.205052 ft]; Body_Flange_Dia=328.95 mm; Body_Flange_Dia_2=337.84 mm; Body_Height_1=312.5 mm; Body_Height_2=156.25 mm; Body_Height_3=125 mm; Body_Height_4=171.25 mm; Body_Top_Dia=39.06 mm; Body_Top_Dia_2=32.55 mm; Body_With_Dia=277.78 mm; Body_With_Dia_2=277.78 mm; Bolt_support=735.29 mm; Bolt_support_2=367.65 mm; Bolt_support_lenght=270.07 mm; Bolt_support_lenght_2=280.07 mm; Bottom_profile=125.04 mm; D1=304.5 mm; DN=500.14 mm; FOD=357.5 mm; Fillet_Length=25 mm  [stored 0.082021 ft]; Flange_thickness=31.5 mm  [stored 0.103346 ft]; H3=1408 mm; ID=250.07 mm; L=1250 mm; L1=1267 mm; L_Ref=1258.5 mm; L_ref_2=563.74 mm; PG_Dia=130 mm; PG_Ref=208.33 mm; PG_ref=260.07 mm; Pilot_Dia_1=83 mm; Pilot_Dia_1_Ref=99.6 mm; Pilot_Dia_1_Ref_2=199.2 mm; Pilot_Dia_2=157.7 mm; Pilot_Dia_3=55.33 mm; Pilot_Dia_4=27.67 mm; Pilot_Dia_5=18.44 mm; Pilot_top_1=839.63 mm; Pilot_top_ref=210.88 mm; Profile1_Height=541 mm; Profile1_Length=111.72 mm; Profile1_Length_2=74.48 mm; Top_Profile=441.18 mm; Top_Profile_Ref=446.18 mm; Top_Ref=628.75 mm; Top_Ref_2=734.19 mm; W=930 mm; W_Ref=772.3 mm
- 879-0500-00-144002372A0_DN500_PN16: A=410.9 mm; Body_Collar_Dia=130.21 mm; Body_Collar_Dia_2=62.5 mm  [stored 0.205052 ft]; Body_Flange_Dia=328.95 mm; Body_Flange_Dia_2=337.84 mm; Body_Height_1=312.5 mm; Body_Height_2=156.25 mm; Body_Height_3=125 mm; Body_Height_4=171.25 mm; Body_Top_Dia=39.06 mm; Body_Top_Dia_2=32.55 mm; Body_With_Dia=277.78 mm; Body_With_Dia_2=277.78 mm; Bolt_support=735.29 mm; Bolt_support_2=367.65 mm; Bolt_support_lenght=270.08 mm; Bolt_support_lenght_2=280.08 mm; Bottom_profile=125.04 mm; D1=304.5 mm; DN=500.16 mm; FOD=357.5 mm; Fillet_Length=25 mm  [stored 0.082021 ft]; Flange_thickness=31.5 mm  [stored 0.103346 ft]; H3=1408 mm; ID=250.08 mm; L=1250 mm; L1=1267 mm; L_Ref=1258.5 mm; L_ref_2=563.74 mm; PG_Dia=130 mm; PG_Ref=208.33 mm; PG_ref=260.08 mm; Pilot_Dia_1=89 mm; Pilot_Dia_1_Ref=106.8 mm; Pilot_Dia_1_Ref_2=213.6 mm; Pilot_Dia_2=169.1 mm; Pilot_Dia_3=59.33 mm; Pilot_Dia_4=29.67 mm; Pilot_Dia_5=19.78 mm; Pilot_top_1=839.63 mm; Pilot_top_ref=210.88 mm; Profile1_Height=563 mm; Profile1_Length=111.72 mm; Profile1_Length_2=74.48 mm; Top_Profile=441.18 mm; Top_Profile_Ref=446.18 mm; Top_Ref=628.75 mm; Top_Ref_2=734.19 mm; W=930 mm; W_Ref=760.9 mm
- 879-0600-00-04400207299_DN600_PN10: A=451.3 mm; Body_Collar_Dia=151.04 mm; Body_Collar_Dia_2=72.5 mm  [stored 0.237861 ft]; Body_Flange_Dia=381.58 mm; Body_Flange_Dia_2=391.89 mm; Body_Height_1=362.5 mm; Body_Height_2=181.25 mm; Body_Height_3=145 mm; Body_Height_4=196.25 mm; Body_Top_Dia=45.31 mm; Body_Top_Dia_2=37.76 mm; Body_With_Dia=322.22 mm; Body_With_Dia_2=322.22 mm; Bolt_support=852.94 mm; Bolt_support_2=426.47 mm; Bolt_support_lenght=320 mm; Bolt_support_lenght_2=330 mm; Bottom_profile=150 mm; D1=341 mm; DN=600 mm; FOD=390 mm; Fillet_Length=30 mm  [stored 0.0984252 ft]; Flange_thickness=36 mm  [stored 0.11811 ft]; H3=1355 mm; ID=300 mm; L=1450 mm; L1=1467 mm; L_Ref=1458.5 mm; L_ref_2=654.48 mm; PG_Dia=150 mm; PG_Ref=241.67 mm; PG_ref=310 mm; Pilot_Dia_1=98 mm; Pilot_Dia_1_Ref=117.6 mm; Pilot_Dia_1_Ref_2=235.2 mm; Pilot_Dia_2=186.2 mm; Pilot_Dia_3=65.33 mm; Pilot_Dia_4=32.67 mm; Pilot_Dia_5=21.78 mm; Pilot_top_1=844.38 mm; Pilot_top_ref=120.63 mm; Profile1_Height=616 mm; Profile1_Length=121.88 mm; Profile1_Length_2=81.25 mm; Top_Profile=511.76 mm; Top_Profile_Ref=516.76 mm; Top_Ref=723.75 mm; Top_Ref_2=784.06 mm; W=1020 mm; W_Ref=833.8 mm
- 879-0600-00-044002072A0_DN600_PN10: A=451.3 mm; Body_Collar_Dia=151.04 mm; Body_Collar_Dia_2=72.5 mm  [stored 0.237861 ft]; Body_Flange_Dia=381.58 mm; Body_Flange_Dia_2=391.89 mm; Body_Height_1=362.5 mm; Body_Height_2=181.25 mm; Body_Height_3=145 mm; Body_Height_4=196.25 mm; Body_Top_Dia=45.31 mm; Body_Top_Dia_2=37.76 mm; Body_With_Dia=322.22 mm; Body_With_Dia_2=322.22 mm; Bolt_support=852.94 mm; Bolt_support_2=426.47 mm; Bolt_support_lenght=320.05 mm; Bolt_support_lenght_2=330.05 mm; Bottom_profile=150.03 mm; D1=341 mm; DN=600.1 mm; FOD=390 mm; Fillet_Length=30 mm  [stored 0.0984252 ft]; Flange_thickness=36 mm  [stored 0.11811 ft]; H3=1518 mm; ID=300.05 mm; L=1450 mm; L1=1467 mm; L_Ref=1458.5 mm; L_ref_2=654.48 mm; PG_Dia=150 mm; PG_Ref=241.67 mm; PG_ref=310.05 mm; Pilot_Dia_1=98 mm; Pilot_Dia_1_Ref=117.6 mm; Pilot_Dia_1_Ref_2=235.2 mm; Pilot_Dia_2=186.2 mm; Pilot_Dia_3=65.33 mm; Pilot_Dia_4=32.67 mm; Pilot_Dia_5=21.78 mm; Pilot_top_1=925.88 mm; Pilot_top_ref=202.13 mm; Profile1_Height=660 mm; Profile1_Length=121.88 mm; Profile1_Length_2=81.25 mm; Top_Profile=511.76 mm; Top_Profile_Ref=516.76 mm; Top_Ref=723.75 mm; Top_Ref_2=824.81 mm; W=1020 mm; W_Ref=833.8 mm
- 879-0600-00-04400217299_DN600_PN10: A=436.1 mm; Body_Collar_Dia=151.04 mm; Body_Collar_Dia_2=72.5 mm  [stored 0.237861 ft]; Body_Flange_Dia=381.58 mm; Body_Flange_Dia_2=391.89 mm; Body_Height_1=362.5 mm; Body_Height_2=181.25 mm; Body_Height_3=145 mm; Body_Height_4=196.25 mm; Body_Top_Dia=45.31 mm; Body_Top_Dia_2=37.76 mm; Body_With_Dia=322.22 mm; Body_With_Dia_2=322.22 mm; Bolt_support=852.94 mm; Bolt_support_2=426.47 mm; Bolt_support_lenght=320.1 mm; Bolt_support_lenght_2=330.1 mm; Bottom_profile=150.05 mm; D1=341 mm; DN=600.2 mm; FOD=390 mm; Fillet_Length=30 mm  [stored 0.0984252 ft]; Flange_thickness=36 mm  [stored 0.11811 ft]; H3=1355 mm; ID=300.1 mm; L=1450 mm; L1=1467 mm; L_Ref=1458.5 mm; L_ref_2=654.48 mm; PG_Dia=150 mm; PG_Ref=241.67 mm; PG_ref=310.1 mm; Pilot_Dia_1=106 mm; Pilot_Dia_1_Ref=127.2 mm; Pilot_Dia_1_Ref_2=254.4 mm; Pilot_Dia_2=201.4 mm; Pilot_Dia_3=70.67 mm; Pilot_Dia_4=35.33 mm; Pilot_Dia_5=23.56 mm; Pilot_top_1=844.38 mm; Pilot_top_ref=120.63 mm; Profile1_Height=616 mm; Profile1_Length=121.88 mm; Profile1_Length_2=81.25 mm; Top_Profile=511.76 mm; Top_Profile_Ref=516.76 mm; Top_Ref=723.75 mm; Top_Ref_2=784.06 mm; W=1020 mm; W_Ref=818.6 mm
- 879-0600-00-044002172A0_DN600_PN10: A=436.1 mm; Body_Collar_Dia=151.04 mm; Body_Collar_Dia_2=72.5 mm  [stored 0.237861 ft]; Body_Flange_Dia=381.58 mm; Body_Flange_Dia_2=391.89 mm; Body_Height_1=362.5 mm; Body_Height_2=181.25 mm; Body_Height_3=145 mm; Body_Height_4=196.25 mm; Body_Top_Dia=45.31 mm; Body_Top_Dia_2=37.76 mm; Body_With_Dia=322.22 mm; Body_With_Dia_2=322.22 mm; Bolt_support=852.94 mm; Bolt_support_2=426.47 mm; Bolt_support_lenght=320.15 mm; Bolt_support_lenght_2=330.15 mm; Bottom_profile=150.08 mm; D1=341 mm; DN=600.3 mm; FOD=390 mm; Fillet_Length=30 mm  [stored 0.0984252 ft]; Flange_thickness=36 mm  [stored 0.11811 ft]; H3=1518 mm; ID=300.15 mm; L=1450 mm; L1=1467 mm; L_Ref=1458.5 mm; L_ref_2=654.48 mm; PG_Dia=150 mm; PG_Ref=241.67 mm; PG_ref=310.15 mm; Pilot_Dia_1=106 mm; Pilot_Dia_1_Ref=127.2 mm; Pilot_Dia_1_Ref_2=254.4 mm; Pilot_Dia_2=201.4 mm; Pilot_Dia_3=70.67 mm; Pilot_Dia_4=35.33 mm; Pilot_Dia_5=23.56 mm; Pilot_top_1=925.88 mm; Pilot_top_ref=202.13 mm; Profile1_Height=660 mm; Profile1_Length=121.88 mm; Profile1_Length_2=81.25 mm; Top_Profile=511.76 mm; Top_Profile_Ref=516.76 mm; Top_Ref=723.75 mm; Top_Ref_2=824.81 mm; W=1020 mm; W_Ref=818.6 mm
- 879-0600-00-04400227299_DN600_PN10: A=451.3 mm; Body_Collar_Dia=151.04 mm; Body_Collar_Dia_2=72.5 mm  [stored 0.237861 ft]; Body_Flange_Dia=381.58 mm; Body_Flange_Dia_2=391.89 mm; Body_Height_1=362.5 mm; Body_Height_2=181.25 mm; Body_Height_3=145 mm; Body_Height_4=196.25 mm; Body_Top_Dia=45.31 mm; Body_Top_Dia_2=37.76 mm; Body_With_Dia=322.22 mm; Body_With_Dia_2=322.22 mm; Bolt_support=852.94 mm; Bolt_support_2=426.47 mm; Bolt_support_lenght=320.2 mm; Bolt_support_lenght_2=330.2 mm; Bottom_profile=150.1 mm; D1=341 mm; DN=600.4 mm; FOD=390 mm; Fillet_Length=30 mm  [stored 0.0984252 ft]; Flange_thickness=36 mm  [stored 0.11811 ft]; H3=1355 mm; ID=300.2 mm; L=1450 mm; L1=1467 mm; L_Ref=1458.5 mm; L_ref_2=654.48 mm; PG_Dia=150 mm; PG_Ref=241.67 mm; PG_ref=310.2 mm; Pilot_Dia_1=98 mm; Pilot_Dia_1_Ref=117.6 mm; Pilot_Dia_1_Ref_2=235.2 mm; Pilot_Dia_2=186.2 mm; Pilot_Dia_3=65.33 mm; Pilot_Dia_4=32.67 mm; Pilot_Dia_5=21.78 mm; Pilot_top_1=844.38 mm; Pilot_top_ref=120.63 mm; Profile1_Height=616 mm; Profile1_Length=121.88 mm; Profile1_Length_2=81.25 mm; Top_Profile=511.76 mm; Top_Profile_Ref=516.76 mm; Top_Ref=723.75 mm; Top_Ref_2=784.06 mm; W=1020 mm; W_Ref=833.8 mm
- 879-0600-00-044002272A0_DN600_PN10: A=451.3 mm; Body_Collar_Dia=151.04 mm; Body_Collar_Dia_2=72.5 mm  [stored 0.237861 ft]; Body_Flange_Dia=381.58 mm; Body_Flange_Dia_2=391.89 mm; Body_Height_1=362.5 mm; Body_Height_2=181.25 mm; Body_Height_3=145 mm; Body_Height_4=196.25 mm; Body_Top_Dia=45.31 mm; Body_Top_Dia_2=37.76 mm; Body_With_Dia=322.22 mm; Body_With_Dia_2=322.22 mm; Bolt_support=852.94 mm; Bolt_support_2=426.47 mm; Bolt_support_lenght=320.25 mm; Bolt_support_lenght_2=330.25 mm; Bottom_profile=150.13 mm; D1=341 mm; DN=600.5 mm; FOD=390 mm; Fillet_Length=30 mm  [stored 0.0984252 ft]; Flange_thickness=36 mm  [stored 0.11811 ft]; H3=1518 mm; ID=300.25 mm; L=1450 mm; L1=1467 mm; L_Ref=1458.5 mm; L_ref_2=654.48 mm; PG_Dia=150 mm; PG_Ref=241.67 mm; PG_ref=310.25 mm; Pilot_Dia_1=98 mm; Pilot_Dia_1_Ref=117.6 mm; Pilot_Dia_1_Ref_2=235.2 mm; Pilot_Dia_2=186.2 mm; Pilot_Dia_3=65.33 mm; Pilot_Dia_4=32.67 mm; Pilot_Dia_5=21.78 mm; Pilot_top_1=925.88 mm; Pilot_top_ref=202.13 mm; Profile1_Height=660 mm; Profile1_Length=121.88 mm; Profile1_Length_2=81.25 mm; Top_Profile=511.76 mm; Top_Profile_Ref=516.76 mm; Top_Ref=723.75 mm; Top_Ref_2=824.81 mm; W=1020 mm; W_Ref=833.8 mm
- 879-0600-00-04400237299_DN600_PN10: A=436.1 mm; Body_Collar_Dia=151.04 mm; Body_Collar_Dia_2=72.5 mm  [stored 0.237861 ft]; Body_Flange_Dia=381.58 mm; Body_Flange_Dia_2=391.89 mm; Body_Height_1=362.5 mm; Body_Height_2=181.25 mm; Body_Height_3=145 mm; Body_Height_4=196.25 mm; Body_Top_Dia=45.31 mm; Body_Top_Dia_2=37.76 mm; Body_With_Dia=322.22 mm; Body_With_Dia_2=322.22 mm; Bolt_support=852.94 mm; Bolt_support_2=426.47 mm; Bolt_support_lenght=320.3 mm; Bolt_support_lenght_2=330.3 mm; Bottom_profile=150.15 mm; D1=341 mm; DN=600.6 mm; FOD=390 mm; Fillet_Length=30 mm  [stored 0.0984252 ft]; Flange_thickness=36 mm  [stored 0.11811 ft]; H3=1355 mm; ID=300.3 mm; L=1450 mm; L1=1467 mm; L_Ref=1458.5 mm; L_ref_2=654.48 mm; PG_Dia=150 mm; PG_Ref=241.67 mm; PG_ref=310.3 mm; Pilot_Dia_1=106 mm; Pilot_Dia_1_Ref=127.2 mm; Pilot_Dia_1_Ref_2=254.4 mm; Pilot_Dia_2=201.4 mm; Pilot_Dia_3=70.67 mm; Pilot_Dia_4=35.33 mm; Pilot_Dia_5=23.56 mm; Pilot_top_1=844.38 mm; Pilot_top_ref=120.63 mm; Profile1_Height=616 mm; Profile1_Length=121.88 mm; Profile1_Length_2=81.25 mm; Top_Profile=511.76 mm; Top_Profile_Ref=516.76 mm; Top_Ref=723.75 mm; Top_Ref_2=784.06 mm; W=1020 mm; W_Ref=818.6 mm
- 879-0600-00-044002372A0_DN600_PN10: A=436.1 mm; Body_Collar_Dia=151.04 mm; Body_Collar_Dia_2=72.5 mm  [stored 0.237861 ft]; Body_Flange_Dia=381.58 mm; Body_Flange_Dia_2=391.89 mm; Body_Height_1=362.5 mm; Body_Height_2=181.25 mm; Body_Height_3=145 mm; Body_Height_4=196.25 mm; Body_Top_Dia=45.31 mm; Body_Top_Dia_2=37.76 mm; Body_With_Dia=322.22 mm; Body_With_Dia_2=322.22 mm; Bolt_support=852.94 mm; Bolt_support_2=426.47 mm; Bolt_support_lenght=320.35 mm; Bolt_support_lenght_2=330.35 mm; Bottom_profile=150.18 mm; D1=341 mm; DN=600.7 mm; FOD=390 mm; Fillet_Length=30 mm  [stored 0.0984252 ft]; Flange_thickness=36 mm  [stored 0.11811 ft]; H3=1518 mm; ID=300.35 mm; L=1450 mm; L1=1467 mm; L_Ref=1458.5 mm; L_ref_2=654.48 mm; PG_Dia=150 mm; PG_Ref=241.67 mm; PG_ref=310.35 mm; Pilot_Dia_1=106 mm; Pilot_Dia_1_Ref=127.2 mm; Pilot_Dia_1_Ref_2=254.4 mm; Pilot_Dia_2=201.4 mm; Pilot_Dia_3=70.67 mm; Pilot_Dia_4=35.33 mm; Pilot_Dia_5=23.56 mm; Pilot_top_1=925.88 mm; Pilot_top_ref=202.13 mm; Profile1_Height=660 mm; Profile1_Length=121.88 mm; Profile1_Length_2=81.25 mm; Top_Profile=511.76 mm; Top_Profile_Ref=516.76 mm; Top_Ref=723.75 mm; Top_Ref_2=824.81 mm; W=1020 mm; W_Ref=818.6 mm
- 879-0600-00-14400207299_DN600_PN16: A=421.3 mm; Body_Collar_Dia=151.04 mm; Body_Collar_Dia_2=72.5 mm  [stored 0.237861 ft]; Body_Flange_Dia=381.58 mm; Body_Flange_Dia_2=391.89 mm; Body_Height_1=362.5 mm; Body_Height_2=181.25 mm; Body_Height_3=145 mm; Body_Height_4=196.25 mm; Body_Top_Dia=45.31 mm; Body_Top_Dia_2=37.76 mm; Body_With_Dia=322.22 mm; Body_With_Dia_2=322.22 mm; Bolt_support=852.94 mm; Bolt_support_2=426.47 mm; Bolt_support_lenght=320.4 mm; Bolt_support_lenght_2=330.4 mm; Bottom_profile=150.2 mm; D1=360 mm; DN=600.8 mm; FOD=420 mm; Fillet_Length=30 mm  [stored 0.0984252 ft]; Flange_thickness=36 mm  [stored 0.11811 ft]; H3=1355 mm; ID=300.4 mm; L=1450 mm; L1=1467 mm; L_Ref=1458.5 mm; L_ref_2=654.48 mm; PG_Dia=150 mm; PG_Ref=241.67 mm; PG_ref=310.4 mm; Pilot_Dia_1=98 mm; Pilot_Dia_1_Ref=117.6 mm; Pilot_Dia_1_Ref_2=235.2 mm; Pilot_Dia_2=186.2 mm; Pilot_Dia_3=65.33 mm; Pilot_Dia_4=32.67 mm; Pilot_Dia_5=21.78 mm; Pilot_top_1=829.38 mm; Pilot_top_ref=105.63 mm; Profile1_Height=616 mm; Profile1_Length=131.25 mm; Profile1_Length_2=87.5 mm; Top_Profile=511.76 mm; Top_Profile_Ref=516.76 mm; Top_Ref=723.75 mm; Top_Ref_2=776.56 mm; W=1020 mm; W_Ref=833.8 mm
- 879-0600-00-144002072A0_DN600_PN16: A=421.3 mm; Body_Collar_Dia=151.04 mm; Body_Collar_Dia_2=72.5 mm  [stored 0.237861 ft]; Body_Flange_Dia=381.58 mm; Body_Flange_Dia_2=391.89 mm; Body_Height_1=362.5 mm; Body_Height_2=181.25 mm; Body_Height_3=145 mm; Body_Height_4=196.25 mm; Body_Top_Dia=45.31 mm; Body_Top_Dia_2=37.76 mm; Body_With_Dia=322.22 mm; Body_With_Dia_2=322.22 mm; Bolt_support=852.94 mm; Bolt_support_2=426.47 mm; Bolt_support_lenght=320.45 mm; Bolt_support_lenght_2=330.45 mm; Bottom_profile=150.23 mm; D1=360 mm; DN=600.9 mm; FOD=420 mm; Fillet_Length=30 mm  [stored 0.0984252 ft]; Flange_thickness=36 mm  [stored 0.11811 ft]; H3=1518 mm; ID=300.45 mm; L=1450 mm; L1=1467 mm; L_Ref=1458.5 mm; L_ref_2=654.48 mm; PG_Dia=150 mm; PG_Ref=241.67 mm; PG_ref=310.45 mm; Pilot_Dia_1=98 mm; Pilot_Dia_1_Ref=117.6 mm; Pilot_Dia_1_Ref_2=235.2 mm; Pilot_Dia_2=186.2 mm; Pilot_Dia_3=65.33 mm; Pilot_Dia_4=32.67 mm; Pilot_Dia_5=21.78 mm; Pilot_top_1=910.88 mm; Pilot_top_ref=187.13 mm; Profile1_Height=660 mm; Profile1_Length=131.25 mm; Profile1_Length_2=87.5 mm; Top_Profile=511.76 mm; Top_Profile_Ref=516.76 mm; Top_Ref=723.75 mm; Top_Ref_2=817.31 mm; W=1020 mm; W_Ref=833.8 mm
- 879-0600-00-14400217299_DN600_PN16: A=406.1 mm; Body_Collar_Dia=151.04 mm; Body_Collar_Dia_2=72.5 mm  [stored 0.237861 ft]; Body_Flange_Dia=381.58 mm; Body_Flange_Dia_2=391.89 mm; Body_Height_1=362.5 mm; Body_Height_2=181.25 mm; Body_Height_3=145 mm; Body_Height_4=196.25 mm; Body_Top_Dia=45.31 mm; Body_Top_Dia_2=37.76 mm; Body_With_Dia=322.22 mm; Body_With_Dia_2=322.22 mm; Bolt_support=852.94 mm; Bolt_support_2=426.47 mm; Bolt_support_lenght=320.06 mm; Bolt_support_lenght_2=330.06 mm; Bottom_profile=150.03 mm; D1=360 mm; DN=600.11 mm; FOD=420 mm; Fillet_Length=30 mm  [stored 0.0984252 ft]; Flange_thickness=36 mm  [stored 0.11811 ft]; H3=1355 mm; ID=300.06 mm; L=1450 mm; L1=1467 mm; L_Ref=1458.5 mm; L_ref_2=654.48 mm; PG_Dia=150 mm; PG_Ref=241.67 mm; PG_ref=310.06 mm; Pilot_Dia_1=106 mm; Pilot_Dia_1_Ref=127.2 mm; Pilot_Dia_1_Ref_2=254.4 mm; Pilot_Dia_2=201.4 mm; Pilot_Dia_3=70.67 mm; Pilot_Dia_4=35.33 mm; Pilot_Dia_5=23.56 mm; Pilot_top_1=829.38 mm; Pilot_top_ref=105.63 mm; Profile1_Height=616 mm; Profile1_Length=131.25 mm; Profile1_Length_2=87.5 mm; Top_Profile=511.76 mm; Top_Profile_Ref=516.76 mm; Top_Ref=723.75 mm; Top_Ref_2=776.56 mm; W=1020 mm; W_Ref=818.6 mm
- 879-0600-00-144002172A0_DN600_PN16: A=406.1 mm; Body_Collar_Dia=151.04 mm; Body_Collar_Dia_2=72.5 mm  [stored 0.237861 ft]; Body_Flange_Dia=381.58 mm; Body_Flange_Dia_2=391.89 mm; Body_Height_1=362.5 mm; Body_Height_2=181.25 mm; Body_Height_3=145 mm; Body_Height_4=196.25 mm; Body_Top_Dia=45.31 mm; Body_Top_Dia_2=37.76 mm; Body_With_Dia=322.22 mm; Body_With_Dia_2=322.22 mm; Bolt_support=852.94 mm; Bolt_support_2=426.47 mm; Bolt_support_lenght=320.06 mm; Bolt_support_lenght_2=330.06 mm; Bottom_profile=150.03 mm; D1=360 mm; DN=600.12 mm; FOD=420 mm; Fillet_Length=30 mm  [stored 0.0984252 ft]; Flange_thickness=36 mm  [stored 0.11811 ft]; H3=1518 mm; ID=300.06 mm; L=1450 mm; L1=1467 mm; L_Ref=1458.5 mm; L_ref_2=654.48 mm; PG_Dia=150 mm; PG_Ref=241.67 mm; PG_ref=310.06 mm; Pilot_Dia_1=106 mm; Pilot_Dia_1_Ref=127.2 mm; Pilot_Dia_1_Ref_2=254.4 mm; Pilot_Dia_2=201.4 mm; Pilot_Dia_3=70.67 mm; Pilot_Dia_4=35.33 mm; Pilot_Dia_5=23.56 mm; Pilot_top_1=910.88 mm; Pilot_top_ref=187.13 mm; Profile1_Height=660 mm; Profile1_Length=131.25 mm; Profile1_Length_2=87.5 mm; Top_Profile=511.76 mm; Top_Profile_Ref=516.76 mm; Top_Ref=723.75 mm; Top_Ref_2=817.31 mm; W=1020 mm; W_Ref=818.6 mm
- 879-0600-00-14400227299_DN600_PN16: A=421.3 mm; Body_Collar_Dia=151.04 mm; Body_Collar_Dia_2=72.5 mm  [stored 0.237861 ft]; Body_Flange_Dia=381.58 mm; Body_Flange_Dia_2=391.89 mm; Body_Height_1=362.5 mm; Body_Height_2=181.25 mm; Body_Height_3=145 mm; Body_Height_4=196.25 mm; Body_Top_Dia=45.31 mm; Body_Top_Dia_2=37.76 mm; Body_With_Dia=322.22 mm; Body_With_Dia_2=322.22 mm; Bolt_support=852.94 mm; Bolt_support_2=426.47 mm; Bolt_support_lenght=320.07 mm; Bolt_support_lenght_2=330.07 mm; Bottom_profile=150.03 mm; D1=360 mm; DN=600.13 mm; FOD=420 mm; Fillet_Length=30 mm  [stored 0.0984252 ft]; Flange_thickness=36 mm  [stored 0.11811 ft]; H3=1355 mm; ID=300.07 mm; L=1450 mm; L1=1467 mm; L_Ref=1458.5 mm; L_ref_2=654.48 mm; PG_Dia=150 mm; PG_Ref=241.67 mm; PG_ref=310.07 mm; Pilot_Dia_1=98 mm; Pilot_Dia_1_Ref=117.6 mm; Pilot_Dia_1_Ref_2=235.2 mm; Pilot_Dia_2=186.2 mm; Pilot_Dia_3=65.33 mm; Pilot_Dia_4=32.67 mm; Pilot_Dia_5=21.78 mm; Pilot_top_1=829.38 mm; Pilot_top_ref=105.63 mm; Profile1_Height=616 mm; Profile1_Length=131.25 mm; Profile1_Length_2=87.5 mm; Top_Profile=511.76 mm; Top_Profile_Ref=516.76 mm; Top_Ref=723.75 mm; Top_Ref_2=776.56 mm; W=1020 mm; W_Ref=833.8 mm
- 879-0600-00-144002272A0_DN600_PN16: A=421.3 mm; Body_Collar_Dia=151.04 mm; Body_Collar_Dia_2=72.5 mm  [stored 0.237861 ft]; Body_Flange_Dia=381.58 mm; Body_Flange_Dia_2=391.89 mm; Body_Height_1=362.5 mm; Body_Height_2=181.25 mm; Body_Height_3=145 mm; Body_Height_4=196.25 mm; Body_Top_Dia=45.31 mm; Body_Top_Dia_2=37.76 mm; Body_With_Dia=322.22 mm; Body_With_Dia_2=322.22 mm; Bolt_support=852.94 mm; Bolt_support_2=426.47 mm; Bolt_support_lenght=320.07 mm; Bolt_support_lenght_2=330.07 mm; Bottom_profile=150.04 mm; D1=360 mm; DN=600.14 mm; FOD=420 mm; Fillet_Length=30 mm  [stored 0.0984252 ft]; Flange_thickness=36 mm  [stored 0.11811 ft]; H3=1518 mm; ID=300.07 mm; L=1450 mm; L1=1467 mm; L_Ref=1458.5 mm; L_ref_2=654.48 mm; PG_Dia=150 mm; PG_Ref=241.67 mm; PG_ref=310.07 mm; Pilot_Dia_1=98 mm; Pilot_Dia_1_Ref=117.6 mm; Pilot_Dia_1_Ref_2=235.2 mm; Pilot_Dia_2=186.2 mm; Pilot_Dia_3=65.33 mm; Pilot_Dia_4=32.67 mm; Pilot_Dia_5=21.78 mm; Pilot_top_1=910.88 mm; Pilot_top_ref=187.13 mm; Profile1_Height=660 mm; Profile1_Length=131.25 mm; Profile1_Length_2=87.5 mm; Top_Profile=511.76 mm; Top_Profile_Ref=516.76 mm; Top_Ref=723.75 mm; Top_Ref_2=817.31 mm; W=1020 mm; W_Ref=833.8 mm
- 879-0600-00-14400237299_DN600_PN16: A=406.1 mm; Body_Collar_Dia=151.04 mm; Body_Collar_Dia_2=72.5 mm  [stored 0.237861 ft]; Body_Flange_Dia=381.58 mm; Body_Flange_Dia_2=391.89 mm; Body_Height_1=362.5 mm; Body_Height_2=181.25 mm; Body_Height_3=145 mm; Body_Height_4=196.25 mm; Body_Top_Dia=45.31 mm; Body_Top_Dia_2=37.76 mm; Body_With_Dia=322.22 mm; Body_With_Dia_2=322.22 mm; Bolt_support=852.94 mm; Bolt_support_2=426.47 mm; Bolt_support_lenght=320.08 mm; Bolt_support_lenght_2=330.08 mm; Bottom_profile=150.04 mm; D1=360 mm; DN=600.15 mm; FOD=420 mm; Fillet_Length=30 mm  [stored 0.0984252 ft]; Flange_thickness=36 mm  [stored 0.11811 ft]; H3=1355 mm; ID=300.08 mm; L=1450 mm; L1=1467 mm; L_Ref=1458.5 mm; L_ref_2=654.48 mm; PG_Dia=150 mm; PG_Ref=241.67 mm; PG_ref=310.08 mm; Pilot_Dia_1=106 mm; Pilot_Dia_1_Ref=127.2 mm; Pilot_Dia_1_Ref_2=254.4 mm; Pilot_Dia_2=201.4 mm; Pilot_Dia_3=70.67 mm; Pilot_Dia_4=35.33 mm; Pilot_Dia_5=23.56 mm; Pilot_top_1=829.38 mm; Pilot_top_ref=105.63 mm; Profile1_Height=616 mm; Profile1_Length=131.25 mm; Profile1_Length_2=87.5 mm; Top_Profile=511.76 mm; Top_Profile_Ref=516.76 mm; Top_Ref=723.75 mm; Top_Ref_2=776.56 mm; W=1020 mm; W_Ref=818.6 mm
- 879-0600-00-144002372A0_DN600_PN16: A=406.1 mm; Body_Collar_Dia=151.04 mm; Body_Collar_Dia_2=72.5 mm  [stored 0.237861 ft]; Body_Flange_Dia=381.58 mm; Body_Flange_Dia_2=391.89 mm; Body_Height_1=362.5 mm; Body_Height_2=181.25 mm; Body_Height_3=145 mm; Body_Height_4=196.25 mm; Body_Top_Dia=45.31 mm; Body_Top_Dia_2=37.76 mm; Body_With_Dia=322.22 mm; Body_With_Dia_2=322.22 mm; Bolt_support=852.94 mm; Bolt_support_2=426.47 mm; Bolt_support_lenght=320.08 mm; Bolt_support_lenght_2=330.08 mm; Bottom_profile=150.04 mm; D1=360 mm; DN=600.16 mm; FOD=420 mm; Fillet_Length=30 mm  [stored 0.0984252 ft]; Flange_thickness=36 mm  [stored 0.11811 ft]; H3=1518 mm; ID=300.08 mm; L=1450 mm; L1=1467 mm; L_Ref=1458.5 mm; L_ref_2=654.48 mm; PG_Dia=150 mm; PG_Ref=241.67 mm; PG_ref=310.08 mm; Pilot_Dia_1=106 mm; Pilot_Dia_1_Ref=127.2 mm; Pilot_Dia_1_Ref_2=254.4 mm; Pilot_Dia_2=201.4 mm; Pilot_Dia_3=70.67 mm; Pilot_Dia_4=35.33 mm; Pilot_Dia_5=23.56 mm; Pilot_top_1=910.88 mm; Pilot_top_ref=187.13 mm; Profile1_Height=660 mm; Profile1_Length=131.25 mm; Profile1_Length_2=87.5 mm; Top_Profile=511.76 mm; Top_Profile_Ref=516.76 mm; Top_Ref=723.75 mm; Top_Ref_2=817.31 mm; W=1020 mm; W_Ref=818.6 mm
- 879-0500-00-044002172A0_DN500_PN10: A=433.4 mm; Body_Collar_Dia=130.21 mm; Body_Collar_Dia_2=62.5 mm  [stored 0.205052 ft]; Body_Flange_Dia=328.95 mm; Body_Flange_Dia_2=337.84 mm; Body_Height_1=312.5 mm; Body_Height_2=156.25 mm; Body_Height_3=125 mm; Body_Height_4=171.25 mm; Body_Top_Dia=39.06 mm; Body_Top_Dia_2=32.55 mm; Body_With_Dia=277.78 mm; Body_With_Dia_2=277.78 mm; Bolt_support=735.29 mm; Bolt_support_2=367.65 mm; Bolt_support_lenght=270.15 mm; Bolt_support_lenght_2=280.15 mm; Bottom_profile=125.08 mm; D1=291 mm; DN=500.3 mm; FOD=335 mm; Fillet_Length=25 mm  [stored 0.082021 ft]; Flange_thickness=31.5 mm  [stored 0.103346 ft]; H3=1408 mm; ID=250.15 mm; L=1250 mm; L1=1267 mm; L_Ref=1258.5 mm; L_ref_2=563.74 mm; PG_Dia=130 mm; PG_Ref=208.33 mm; PG_ref=260.15 mm; Pilot_Dia_1=89 mm; Pilot_Dia_1_Ref=106.8 mm; Pilot_Dia_1_Ref_2=213.6 mm; Pilot_Dia_2=169.1 mm; Pilot_Dia_3=59.33 mm; Pilot_Dia_4=29.67 mm; Pilot_Dia_5=19.78 mm; Pilot_top_1=850.88 mm; Pilot_top_ref=222.13 mm; Profile1_Height=563 mm; Profile1_Length=104.69 mm; Profile1_Length_2=69.79 mm; Top_Profile=441.18 mm; Top_Profile_Ref=446.18 mm; Top_Ref=628.75 mm; Top_Ref_2=739.81 mm; W=930 mm; W_Ref=760.9 mm
- 879-0500-00-14400237299_DN500_PN16: A=410.9 mm; Body_Collar_Dia=130.21 mm; Body_Collar_Dia_2=62.5 mm  [stored 0.205052 ft]; Body_Flange_Dia=328.95 mm; Body_Flange_Dia_2=337.84 mm; Body_Height_1=312.5 mm; Body_Height_2=156.25 mm; Body_Height_3=125 mm; Body_Height_4=171.25 mm; Body_Top_Dia=39.06 mm; Body_Top_Dia_2=32.55 mm; Body_With_Dia=277.78 mm; Body_With_Dia_2=277.78 mm; Bolt_support=735.29 mm; Bolt_support_2=367.65 mm; Bolt_support_lenght=270.08 mm; Bolt_support_lenght_2=280.08 mm; Bottom_profile=125.04 mm; D1=304.5 mm; DN=500.15 mm; FOD=357.5 mm; Fillet_Length=25 mm  [stored 0.082021 ft]; Flange_thickness=31.5 mm  [stored 0.103346 ft]; H3=1245 mm; ID=250.08 mm; L=1250 mm; L1=1267 mm; L_Ref=1258.5 mm; L_ref_2=563.74 mm; PG_Dia=130 mm; PG_Ref=208.33 mm; PG_ref=260.08 mm; Pilot_Dia_1=89 mm; Pilot_Dia_1_Ref=106.8 mm; Pilot_Dia_1_Ref_2=213.6 mm; Pilot_Dia_2=169.1 mm; Pilot_Dia_3=59.33 mm; Pilot_Dia_4=29.67 mm; Pilot_Dia_5=19.78 mm; Pilot_top_1=758.13 mm; Pilot_top_ref=129.38 mm; Profile1_Height=541 mm; Profile1_Length=111.72 mm; Profile1_Length_2=74.48 mm; Top_Profile=441.18 mm; Top_Profile_Ref=446.18 mm; Top_Ref=628.75 mm; Top_Ref_2=693.44 mm; W=930 mm; W_Ref=760.9 mm

note: [stored X ft] marks values corroborated as IEEE doubles in the binary element streams (Revit-internal decimal feet)

## geometry (parser evidence)
native form markers: Sweep x6
no freeform markers — native parametric forms only
